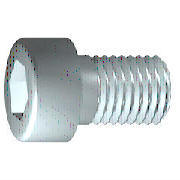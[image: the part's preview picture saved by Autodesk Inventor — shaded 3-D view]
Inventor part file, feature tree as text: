
AUTODESK INVENTOR PART (.ipt)
format: ipt  version: 2015 (Build 190159000, 159)  size: 195,584 bytes
history: native  units: mm (DEFAULTED — no unit token found)
features: sketch x2, extrude x1, plane x1, fillet x1
ambient origin geometry x7: Origin, YZ Plane, XY Plane, X Axis, Y Axis, Z Axis, Center Point
bodies: Solid1 (feature_tree), Body (feature_tree)
feature tree (5):
  extrude  "Slot"  Depth=8.0mm
  plane  "Work Plane1"
  fillet  "Fillet2"  Radius=8.0mm
  sketch  "Sketch1"  dims[d1=26.875mm d2=0.766912mm d3=8.0mm]
  sketch  "Sketch2"  dims[d4=4.0mm d5=60.0deg d6=8.0mm d7=8.0mm d8=6.928203mm d9=13.0mm d10=90.0deg d11=10.0mm d12=0.0mm d13=26.875mm d14=0.0mm d15=0.766813mm d16=0.766813mm d17=0.8mm d19=0.0mm d26=30.0mm d27=45.0deg d28=0.0mm d29=0.0mm d30=0.1mm]
